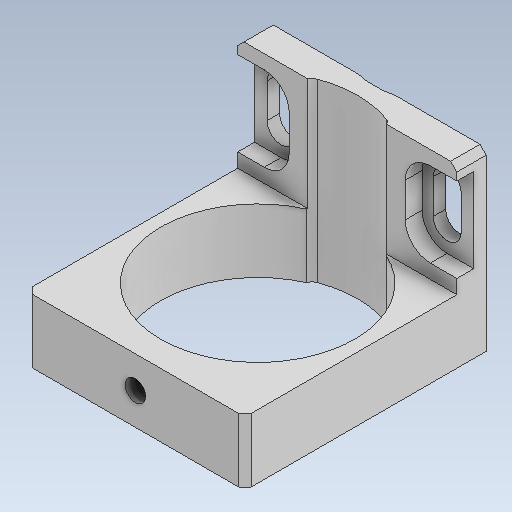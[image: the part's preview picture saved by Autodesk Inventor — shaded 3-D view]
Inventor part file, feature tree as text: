
AUTODESK INVENTOR PART (.ipt)
format: ipt  version: 2020 (Build 240168000, 168)  size: 445,952 bytes
history: native  units: in
note: dims shown in document units (in); Inventor stores cm internally (conversion verified against a paired STEP export)
features: extrude x8, sketch x8, hole x2, chamfer x1
ambient origin geometry x8: Origin, YZ Plane, XZ Plane, XY Plane, X Axis, Y Axis, Z Axis, Center Point
bodies: Body1 (feature_tree)
feature tree (19):
  extrude  "Extrusion3"  Depth=0.6906in
  extrude  "Extrusion4"  Depth=0.185in TaperAngle=0.0deg
  sketch  "Sketch9"  dims[d31=0.0in d32=0.0in]
  extrude  "Extrusion6"  TaperAngle=0.0deg  [1 undecoded]
  extrude  "Extrusion7"  TaperAngle=0.0deg  [1 undecoded]
  hole  "Hole3"  [1 undecoded]
  chamfer  "Chamfer10"  Distance=0.3622in
  extrude  "Extrusion11"  Depth=0.7087in
  hole  "Hole4"  [1 undecoded]
  extrude  "Extrusion15"  TaperAngle=0.0deg  [1 undecoded]
  extrude  "Extrusion16"  Depth=0.6906in
  extrude  "Extrusion19"  Depth=0.6906in
  sketch  "Sketch4"  dims[d24=1.1102in d26=0.6906in]
  sketch  "Sketch5"  dims[d28=0.4016in d29=0.185in d30=0.0in]
  sketch  "Sketch13"  dims[d33=0.0in d34=0.0in]
  sketch  "Sketch14"  dims[d35=1.3358in d36=0.0in d77=0.0827in d78=0.0in]
  sketch  "Sketch20"  dims[d85=0.0827in d86=0.328in d87=0.297in d88=0.11in d89=90.0deg d90=0.0827in d91=0.0in d93=0.3622in d94=0.0in]
  sketch  "Sketch21"  dims[d131=0.3543in d183=0.7087in]
  sketch  "Sketch26"  dims[d185=0.0886in d186=0.2165in d187=0.0in d188=0.3243in d189=0.0413in d190=0.0392in d191=0.0in d192=0.1969in d193=0.0394in d194=0.0787in d195=45.0deg d196=0.0in d197=1.0in d199=0.3937in d200=0.0in d201=0.75in d203=0.0in d204=0.1969in d205=0.13in d206=0.328in d207=0.1575in d208=0.0787in d209=90.0deg d211=0.0in d212=0.0in d213=0.2008in d214=0.4016in d224=0.4862in d225=0.6906in d226=1.2433in d227=0.1374in d228=0.1374in d229=0.1201in d230=0.1201in d231=0.5616in d232=0.5616in d251=0.7087in d252=0.3543in d253=0.4827in d254=0.1673in d255=0.1772in d256=0.2165in d257=0.7087in d258=0.4827in d259=0.3543in d261=0.1772in d262=0.2165in d263=0.0in d264=0.0in d265=0.3543in d266=0.1673in d267=0.3543in d269=0.315in d270=0.2165in d271=0.315in d272=0.2165in d273=0.1063in d274=0.0in d293=0.1673in d295=0.1673in d309=0.75in d311=0.002in d314=1.2236in d315=0.75in d316=0.6906in d317=1.263in d318=0.1374in d319=0.1374in d320=0.1201in d321=0.1201in d322=0.5715in d323=0.5715in d324=0.75in d325=1.374in d326=0.002in d327=0.0in d328=0.0in]
note: 5 required parameter values undecoded (feature->parameter linkage not recoverable at this tier; creation-order binding heuristic only, values carry confidence <= 0.55)
